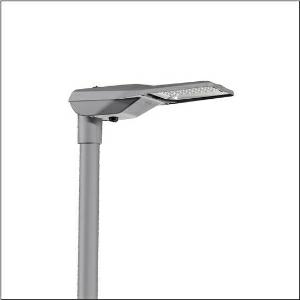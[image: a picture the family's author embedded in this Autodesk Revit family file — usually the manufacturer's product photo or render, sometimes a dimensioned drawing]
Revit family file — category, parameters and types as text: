
# Revit family: streetlight_sl_21_mini___st0_8a_5xe2c33t08jb_bac6
name_source: partatom
category: Lighting Fixtures
units: mm (PartAtom-declared; Revit-internal decimal feet)

## family parameters
Cut with Voids When Loaded = No
Host = Face
Light Source = No
Part Type = Normal
Room Calculation Point = No
Round Connector Dimension = Use Diameter
Shared = No

## types (1)
- --- (1 x LED, 12940 lm, 88.6 W, 3000K)
    Apparent Load = 89 VA
    CIE Flux Codes = 41 75 97 100 100
    Color Rendering = 70
    Color Temperature = 3000K
    Default Elevation = 1800 mm
    Description = Streetlight SL 21 mini, mast luminaire, primary light control with lens, of PMMA, primary optical cover: cover, of toughened safety glass, transparent, light distribution: ST0.8a, light emission: direct distribution, primary light characteristic: asymmetric, installation type: side-entry, post-top, LED, High Power LED, rated luminous flux: 12.940lm, luminous efficacy: 146lm/W, light colour: 730, colour temperature: 3000K, control gear: D4i, control: overheat protection, constant luminous flux control, time-dependent luminous flux control, flexible luminous flux parameterisation, pre-setting: logarithmic dimming characteristic, mains connection: 220..240V, AC, 50/60Hz, start of lifetime: 89W, end of service life: 92W, reduction: 41W, luminaire housing, of diecast aluminium, powder-coated, SITECO metallic grey (DB 702S), corrosivity category C5 high according to DIN EN ISO 12944, please order mast flange separately, inclination adjustable: 0°, 5°, 10°, 15°, sealing non-destructively replaceable, multi-level sealing system, length: 628mm, width: 235mm, height: 110mm, mast flange for spigot size: 42mm (side-entry): 5XC10008XM4, 60/48mm (side-entry/post-top): 5XC10108XM2, 76/60mm (side-entry/post-top): 5XC10108XM1, mounting height: 4..8m, Smart Interface below and above, protection rating (complete): IP66, insulation class (complete): insulation class II (safety insulation), certification: CE, ENEC, ENEC+, VDE, impact resistance: IK10, permissible operating ambient temperature for outdoor applications: -40..+50°C, standard-compliant lighting for roads and squares, packaging unit: 1 piece

Light Distribution: ST0.8a
    Height = 110 mm
    Lamp = 1 x LED
    Lamp Light Flux = 12940 lm
    Lamp Power = 88.6 W
    Lamp count = 1
    Length = 625 mm
    Luminous efficacy = 146 lm/W
    Manufacturer = Siteco
    ModVariant = No
    Model = 5XE2C33T08JB
    Number of Poles = 1
    OnlyDefault = Yes
    Power Factor = 1
    Product Name = Streetlight SL 21 mini | ST0.8a
    Product group = mast luminaire | pylon top
    ProductGroupID = 6100
    Protection Class = Protection class II
    Protection Degree = IP 66
    RLX_Detail_Level = 1
    RLX_Emergency_Light_Flux = 0 lm
    RLX_Emergency_Type = 0
    RLX_Emergency_Type_DB = No
    RlxData = <blob elided: 26357 chars, md5=c2fe2574>
    Socket = socket
    Standby Power = 0 W
    System Light Flux = 12940 lm
    System Power = 89 W
    Type Comments = factory setting: luminous flux: 100 % | dim-lin: 254 | 915 mA
    Type Image = l_1003514.jpg
    URL = http://relux.com
    VarID = @adj_030703
    Voltage = 0 V
    Weight = 0.00 kg
    Width = 234 mm

## geometry (parser evidence)
native form markers: Blend x4, Sweep x11
no freeform markers — native parametric forms only
